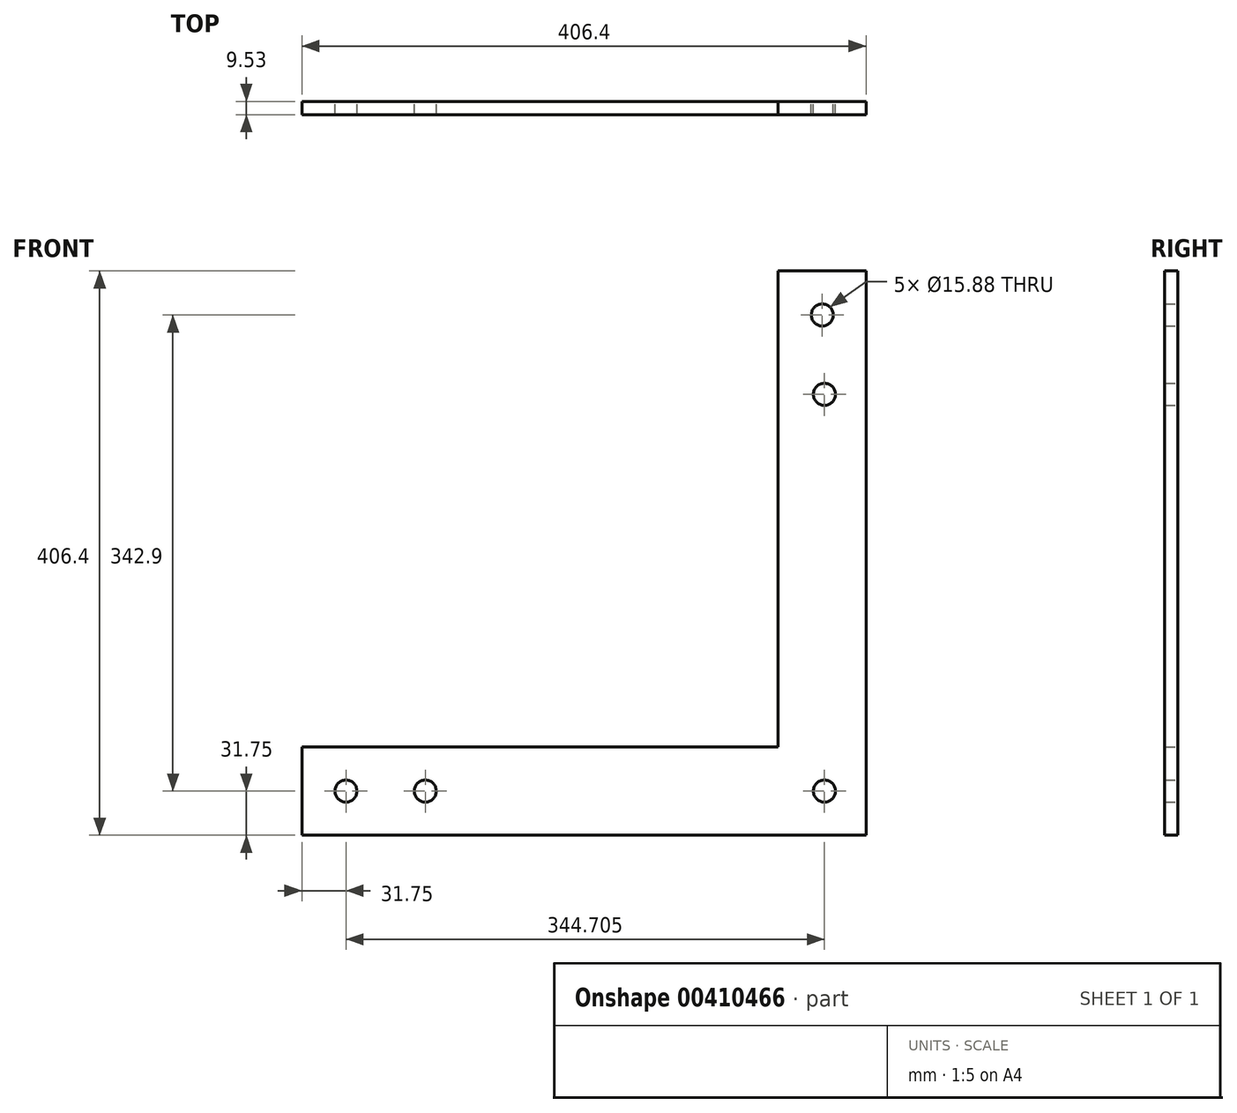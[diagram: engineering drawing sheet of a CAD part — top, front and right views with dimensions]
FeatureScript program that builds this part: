
annotation { "Feature Type Name" : "Feature", "Feature Type Description" : "" }
export const myFeature = defineFeature(function(context is Context, id is Id, definition is map)
    precondition{}
    {
        {
            var Q0;
            Q0=qCreatedBy(makeId("Front.planeOp"),FACE);
            var sketch = newSketch(context, id + "F0", { "sketchPlane" : qUnion([Q0])});
            skLineSegment(sketch, "E0.bottom", {"start": v(-203.2, 31.75) * mm, "end": v(203.2, 31.75) * mm});
            skLineSegment(sketch, "E0.top", {"start": v(-203.2, -31.75) * mm, "end": v(203.2, -31.75) * mm});
            skLineSegment(sketch, "E0.left", {"start": v(-203.2, 31.75) * mm, "end": v(-203.2, -31.75) * mm});
            skLineSegment(sketch, "E0.right", {"start": v(203.2, 31.75) * mm, "end": v(203.2, -31.75) * mm});
            skPoint(sketch, "E0.middle", {"position": v(0, 0) * mm});
            skLineSegment(sketch, "E1.bottom", {"start": v(203.2, 31.75) * mm, "end": v(139.7, 31.75) * mm});
            skLineSegment(sketch, "E1.top", {"start": v(203.2, 374.65) * mm, "end": v(139.7, 374.65) * mm});
            skLineSegment(sketch, "E1.left", {"start": v(203.2, 31.75) * mm, "end": v(203.2, 374.65) * mm});
            skLineSegment(sketch, "E1.right", {"start": v(139.7, 31.75) * mm, "end": v(139.7, 374.65) * mm});
            skCircle(sketch, "E2", {"center": v(-171.45, 0) * mm, "radius": 7.94 * mm});
            skCircle(sketch, "E3", {"center": v(-114.3, 0) * mm, "radius": 7.94 * mm});
            skCircle(sketch, "E4", {"center": v(173.26, 0) * mm, "radius": 7.94 * mm});
            skCircle(sketch, "E5", {"center": v(171.71, 342.9) * mm, "radius": 7.94 * mm});
            skCircle(sketch, "E6", {"center": v(173.26, 285.75) * mm, "radius": 7.94 * mm});
            skSolve(sketch);
        }
        {
            var Q0;
            Q0 = qSketchRegion(id + "F0", true);
            extrude(context, id + "F1", {"entities" : qUnion([Q0]), "depth" : 9.52 * mm, "offsetDistance" : 25.4 * mm});
        }
    });
